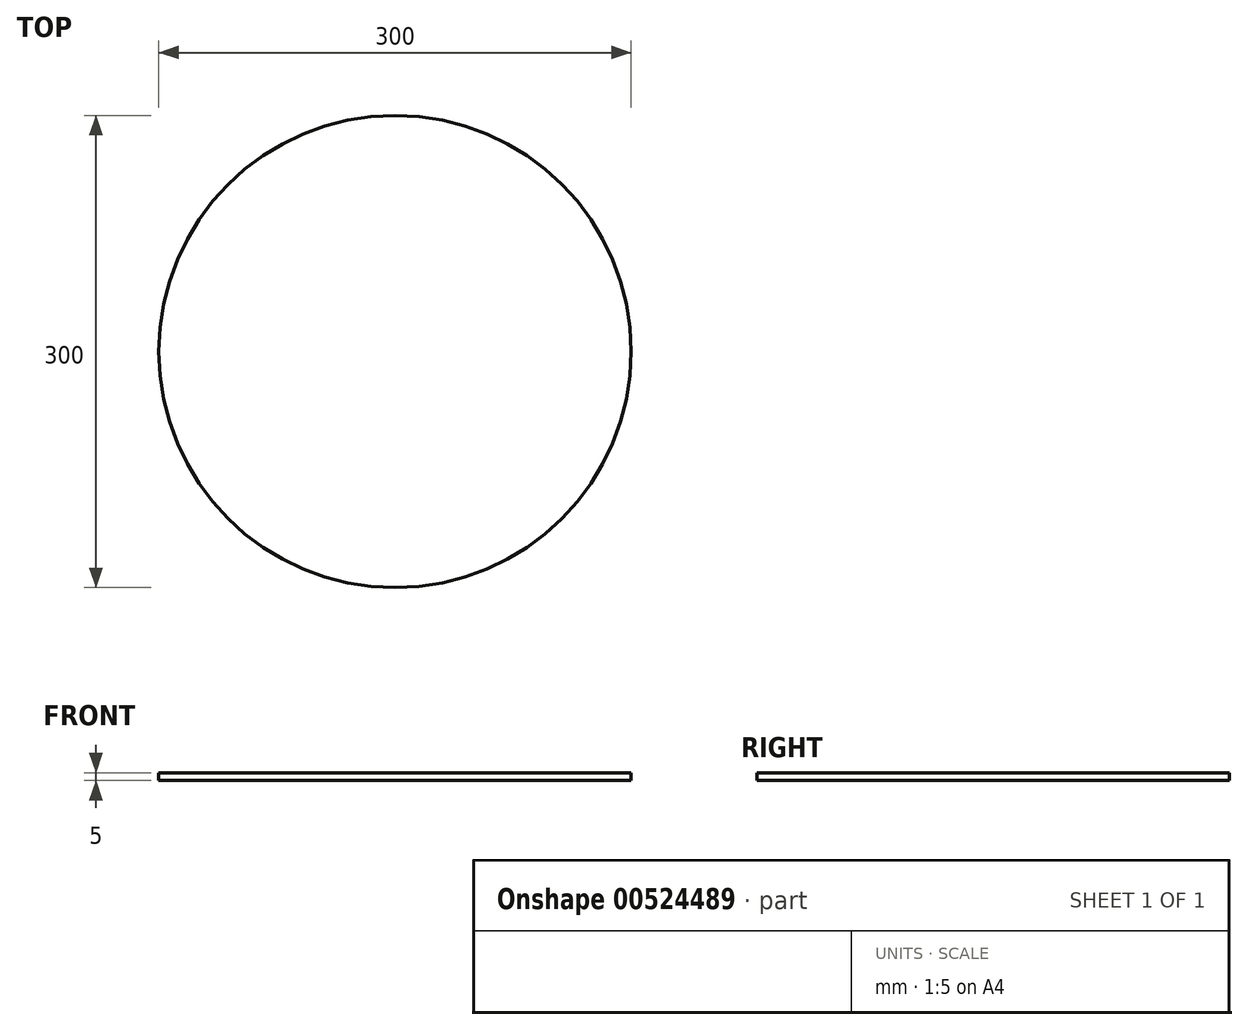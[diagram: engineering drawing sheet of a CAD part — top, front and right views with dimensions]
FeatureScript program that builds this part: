
annotation { "Feature Type Name" : "Feature", "Feature Type Description" : "" }
export const myFeature = defineFeature(function(context is Context, id is Id, definition is map)
    precondition{}
    {
        {
            assignVariable(context, id + "F0", {"name" : "discThickness", "anyValue" : 5 * mm});
        }
        {
            var Q0;
            Q0=qCreatedBy(makeId("Top.planeOp"),FACE);
            var sketch = newSketch(context, id + "F1", { "sketchPlane" : qUnion([Q0])});
            skCircle(sketch, "E0", {"center": v(0, 0) * mm, "radius": 150 * mm});
            skSolve(sketch);
        }
        {
            var Q0;
            Q0 = qSketchRegion(id + "F1", true);
            extrude(context, id + "F2", {"entities" : qUnion([Q0]), "oppositeDirection" : true, "depth" : getVariable(context, 'discThickness'), "offsetDistance" : 25 * mm});
        }
    });
